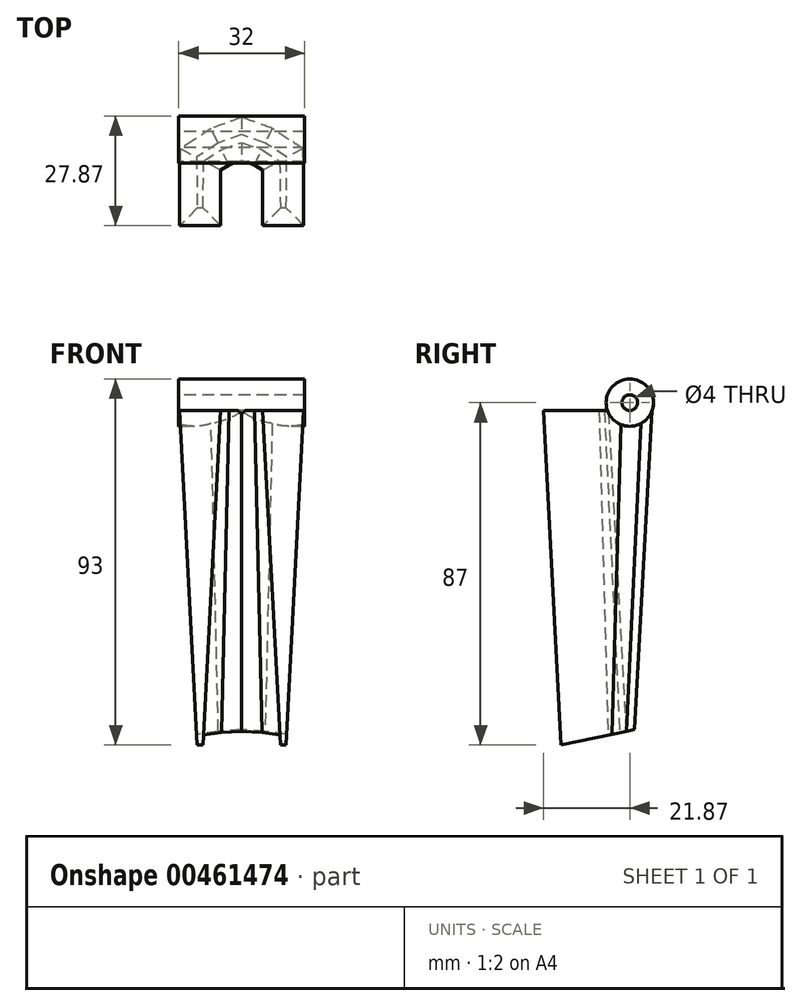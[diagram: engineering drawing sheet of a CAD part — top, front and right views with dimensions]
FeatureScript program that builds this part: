
annotation { "Feature Type Name" : "Feature", "Feature Type Description" : "" }
export const myFeature = defineFeature(function(context is Context, id is Id, definition is map)
    precondition{}
    {
        {
            var Q0;
            Q0=qCreatedBy(makeId("Top.planeOp"),FACE);
            var sketch = newSketch(context, id + "F0", { "sketchPlane" : qUnion([Q0])});
            skLineSegment(sketch, "E0", {"start": v(0, 0) * mm, "end": v(0, 12) * mm});
            skLineSegment(sketch, "E1", {"start": v(0, 12) * mm, "end": v(4.6, 15) * mm});
            skLineSegment(sketch, "E2", {"start": v(4.6, 15) * mm, "end": v(9.8, 16.8) * mm});
            skLineSegment(sketch, "E3", {"start": v(9.8, 16.8) * mm, "end": v(9.8, 19.65) * mm, "construction": true});
            skLineSegment(sketch, "E4.MirrorCS", {"start": v(15, 15) * mm, "end": v(9.8, 16.8) * mm});
            skLineSegment(sketch, "E5.MirrorCS", {"start": v(19.61, 12) * mm, "end": v(15, 15) * mm});
            skLineSegment(sketch, "E6.MirrorCS", {"start": v(19.61, 0) * mm, "end": v(19.61, 12) * mm});
            skLineSegment(sketch, "E7.0", {"start": v(3.95, 16.36) * mm, "end": v(9.32, 18.22) * mm});
            skLineSegment(sketch, "E7.1", {"start": v(-1.5, 12.81) * mm, "end": v(3.95, 16.36) * mm});
            skLineSegment(sketch, "E7.2", {"start": v(-1.5, 0) * mm, "end": v(-1.5, 12.81) * mm});
            skLineSegment(sketch, "E8.MirrorCS", {"start": v(15.67, 16.36) * mm, "end": v(10.29, 18.22) * mm});
            skLineSegment(sketch, "E9.MirrorCS", {"start": v(21.11, 12.81) * mm, "end": v(15.67, 16.36) * mm});
            skLineSegment(sketch, "E10.MirrorCS", {"start": v(21.11, 0) * mm, "end": v(21.11, 12.81) * mm});
            skLineSegment(sketch, "E11", {"start": v(10.29, 18.22) * mm, "end": v(9.8, 18.39) * mm});
            skLineSegment(sketch, "E12", {"start": v(9.8, 18.39) * mm, "end": v(9.32, 18.22) * mm});
            skLineSegment(sketch, "E13", {"start": v(-1.5, 0) * mm, "end": v(0, 0) * mm});
            skLineSegment(sketch, "E14", {"start": v(19.61, 0) * mm, "end": v(21.11, 0) * mm});
            skSolve(sketch);
        }
        {
            var Q0;
            Q0=qCreatedBy(makeId("Top.planeOp"),FACE);
            cPlane(context, id + "F1", {"entities" : qUnion([Q0]), "cplaneType" : CPlaneType.OFFSET, "offset" : 85 * mm, "width" : 150 * mm, "height" : 150 * mm});
        }
        {
            var Q0;
            Q0 = qSketchRegion(id + "F0", true);
            extrude(context, id + "F2", {"entities" : qUnion([Q0]), "depth" : 85 * mm, "hasDraft" : true, "draftAngle" : 3 * degree});
        }
        {
            var Q0;
            Q0=makeQuery(id+"F2.opExtrude","CAP_FACE",FACE,{"disambiguationData":[OSD([sQuery(id+"F0.wireOp",EDGE,"E0"),sQuery(id+"F0.wireOp",EDGE,"E1"),sQuery(id+"F0.wireOp",EDGE,"E2"),sQuery(id+"F0.wireOp",EDGE,"E4.MirrorCS"),sQuery(id+"F0.wireOp",EDGE,"E5.MirrorCS"),sQuery(id+"F0.wireOp",EDGE,"E6.MirrorCS"),sQuery(id+"F0.wireOp",EDGE,"E7.0"),sQuery(id+"F0.wireOp",EDGE,"E7.1"),sQuery(id+"F0.wireOp",EDGE,"E7.2"),sQuery(id+"F0.wireOp",EDGE,"E8.MirrorCS"),sQuery(id+"F0.wireOp",EDGE,"E9.MirrorCS"),sQuery(id+"F0.wireOp",EDGE,"E10.MirrorCS"),sQuery(id+"F0.wireOp",EDGE,"E11"),sQuery(id+"F0.wireOp",EDGE,"E12"),sQuery(id+"F0.wireOp",EDGE,"E13"),sQuery(id+"F0.wireOp",EDGE,"E14")])],"isStart":false});
            var sketch = newSketch(context, id + "F3", { "sketchPlane" : qUnion([Q0])});
            skLineSegment(sketch, "E15", {"start": v(9.8, 12.09) * mm, "end": v(8.8, 12.09) * mm});
            skLineSegment(sketch, "E16", {"start": v(8.8, 12.09) * mm, "end": v(8.8, 22.76) * mm});
            skLineSegment(sketch, "E17", {"start": v(8.8, 22.76) * mm, "end": v(10.8, 22.76) * mm});
            skLineSegment(sketch, "E18", {"start": v(10.8, 22.76) * mm, "end": v(10.8, 12.09) * mm});
            skLineSegment(sketch, "E19", {"start": v(10.8, 12.09) * mm, "end": v(9.8, 12.09) * mm});
            skSolve(sketch);
        }
        {
            var Q0;
            Q0 = qSketchRegion(id + "F3", true);
            extrude(context, id + "F4", {"entities" : qUnion([Q0]), "operationType" : NewBodyOperationType.ADD, "depth" : 1 * mm});
        }
        {
            var Q0;
            Q0=makeQuery(id+"F4.opExtrude","SWEPT_FACE",FACE,{"disambiguationData":[OSD([sQuery(id+"F3.wireOp",EDGE,"E18")])]});
            var sketch = newSketch(context, id + "F5", { "sketchPlane" : qUnion([Q0])});
            skLineSegment(sketch, "E20", {"start": v(17.42, 85) * mm, "end": v(17.42, 87) * mm, "construction": true});
            skCircle(sketch, "E21", {"center": v(17.42, 87) * mm, "radius": 6 * mm});
            skCircle(sketch, "E22", {"center": v(17.42, 87) * mm, "radius": 2 * mm});
            skSolve(sketch);
        }
        {
            var Q0;
            Q0 = qSketchRegion(id + "F5", true);
            extrude(context, id + "F6", {"entities" : qUnion([Q0]), "operationType" : NewBodyOperationType.ADD, "depth" : 15 * mm, "hasSecondDirection" : true, "secondDirectionOppositeDirection" : true, "secondDirectionDepth" : 17 * mm});
        }
        {
            var Q0;
            Q0=makeQuery(id+"F6.opExtrude","CAP_FACE",FACE,{"disambiguationData":[OSD([sQuery(id+"F5.wireOp",EDGE,"E21"),sQuery(id+"F5.wireOp",EDGE,"E22")])],"isStart":false});
            var sketch = newSketch(context, id + "F7", { "sketchPlane" : qUnion([Q0])});
            skCircle(sketch, "E23", {"center": v(17.42, 87) * mm, "radius": 2 * mm});
            skSolve(sketch);
        }
        {
            var Q0;
            Q0 = qSketchRegion(id + "F7", true);
            extrude(context, id + "F8", {"entities" : qUnion([Q0]), "operationType" : NewBodyOperationType.REMOVE, "oppositeDirection" : true, "depth" : 25 * mm});
        }
        {
            var Q0;
            Q0=qCreatedBy(makeId("Right.planeOp"),FACE);
            cPlane(context, id + "F9", {"entities" : qUnion([Q0]), "cplaneType" : CPlaneType.OFFSET, "offset" : 9.8 * mm, "width" : 150 * mm, "height" : 150 * mm});
        }
        {
            var Q0;
            Q0=qCreatedBy(id+"F9.planeOp",FACE);
            var sketch = newSketch(context, id + "F10", { "sketchPlane" : qUnion([Q0])});
            skLineSegment(sketch, "E24", {"start": v(0, 0) * mm, "end": v(20.41, 0) * mm});
            skLineSegment(sketch, "E25", {"start": v(0, 0) * mm, "end": v(20.41, 4.34) * mm});
            skLineSegment(sketch, "E26", {"start": v(20.41, 4.34) * mm, "end": v(20.41, 0) * mm});
            skSolve(sketch);
        }
        {
            var Q0;
            Q0 = qSketchRegion(id + "F10", true);
            extrude(context, id + "F11", {"entities" : qUnion([Q0]), "operationType" : NewBodyOperationType.REMOVE, "oppositeDirection" : true, "depth" : 25 * mm, "hasSecondDirection" : true, "secondDirectionOppositeDirection" : false, "secondDirectionDepth" : 25 * mm});
        }
    });
